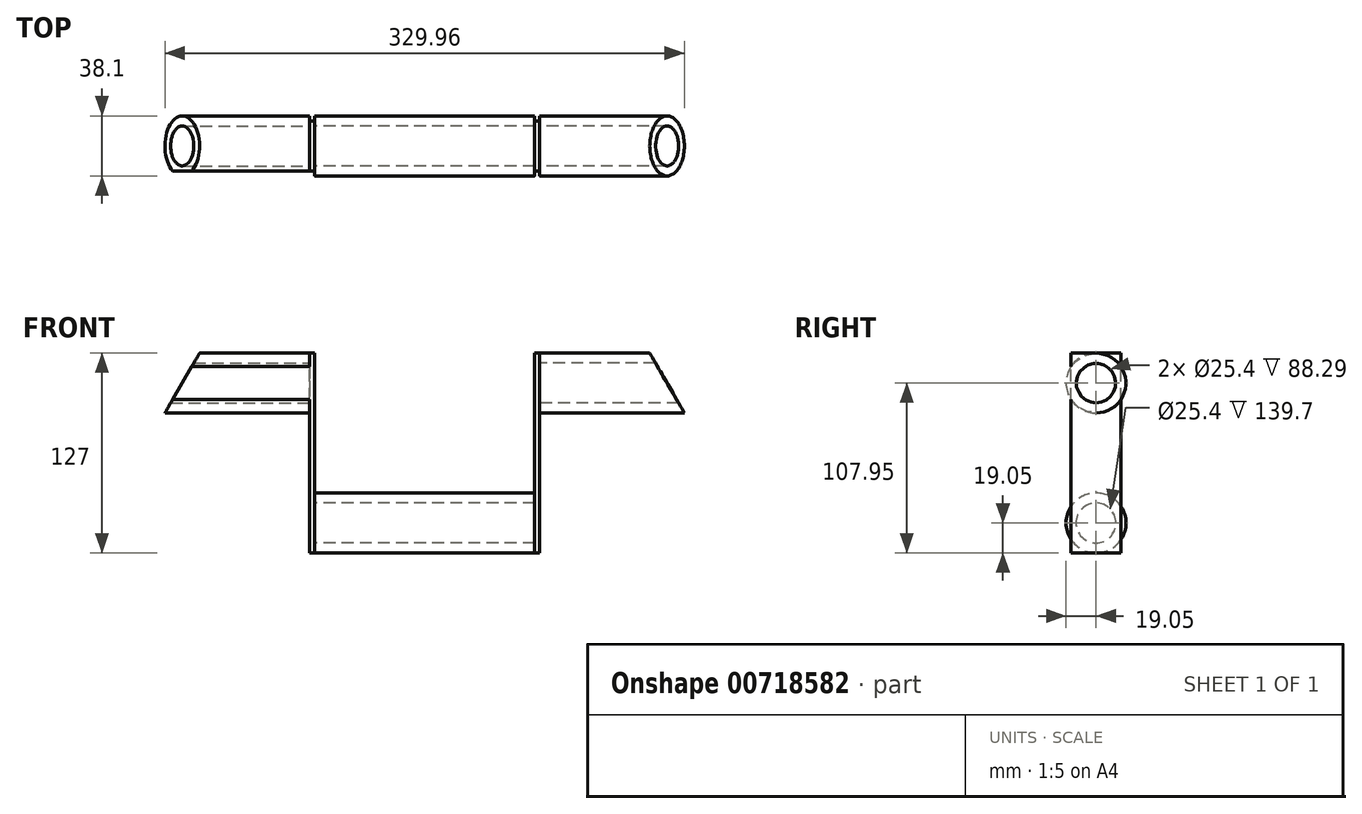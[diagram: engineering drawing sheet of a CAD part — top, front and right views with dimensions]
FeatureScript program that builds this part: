
annotation { "Feature Type Name" : "Feature", "Feature Type Description" : "" }
export const myFeature = defineFeature(function(context is Context, id is Id, definition is map)
    precondition{}
    {
        {
            var Q0;
            Q0=qCreatedBy(makeId("Right.planeOp"),FACE);
            var sketch = newSketch(context, id + "F0", { "sketchPlane" : qUnion([Q0])});
            skCircle(sketch, "E0", {"center": v(0, 0) * mm, "radius": 19.05 * mm});
            skCircle(sketch, "E1", {"center": v(0, 0) * mm, "radius": 12.7 * mm});
            skSolve(sketch);
        }
        {
            var Q0;
            Q0=qCreatedBy(makeId("Front.planeOp"),FACE);
            var sketch = newSketch(context, id + "F1", { "sketchPlane" : qUnion([Q0])});
            skLineSegment(sketch, "E2", {"start": v(0, 0) * mm, "end": v(153.98, 88.9) * mm});
            skLineSegment(sketch, "E3", {"start": v(153.98, 88.9) * mm, "end": v(0, 0) * mm});
            skLineSegment(sketch, "E4", {"start": v(0, 0) * mm, "end": v(-153.98, 88.9) * mm});
            skSolve(sketch);
        }
        {
            var Q0;
            Q0=makeQuery(id+"F0.imprint","IMPRINT",FACE,{"disambiguationData":[TD([[makeQuery(id+"F0.imprint","IMPRINT",EDGE,{"derivedFrom":sQuery(id+"F0.wireOp",EDGE,"E0")}),1.0]])]});
            extrude(context, id + "F2", {"entities" : qUnion([Q0]), "endBound" : BoundingType.SYMMETRIC, "depth" : 139.7 * mm, "offsetDistance" : 25.4 * mm});
        }
        {
            var Q0;
            Q0=makeQuery(id+"F2.opExtrude","CAP_FACE",FACE,{"disambiguationData":[OSD([sQuery(id+"F0.wireOp",EDGE,"E0"),sQuery(id+"F0.wireOp",EDGE,"E1")])],"isStart":false});
            var sketch = newSketch(context, id + "F3", { "sketchPlane" : qUnion([Q0])});
            skLineSegment(sketch, "E5.bottom", {"start": v(15.88, -19.05) * mm, "end": v(-15.88, -19.05) * mm});
            skPoint(sketch, "E5.middle", {"position": v(0, 0) * mm});
            skLineSegment(sketch, "E6", {"start": v(-15.88, -19.05) * mm, "end": v(-15.88, 107.95) * mm});
            skLineSegment(sketch, "E7", {"start": v(15.88, -19.05) * mm, "end": v(15.88, 107.95) * mm});
            skLineSegment(sketch, "E8", {"start": v(-15.88, 107.95) * mm, "end": v(15.88, 107.95) * mm});
            skSolve(sketch);
        }
        {
            var Q0;
            Q0 = qSketchRegion(id + "F3", true);
            extrude(context, id + "F4", {"entities" : qUnion([Q0]), "operationType" : NewBodyOperationType.ADD, "depth" : 3.17 * mm, "offsetDistance" : 25.4 * mm});
        }
        {
            var Q0;
            Q0=makeQuery(id+"F4.opExtrude","CAP_FACE",FACE,{"disambiguationData":[OSD([sQuery(id+"F3.wireOp",EDGE,"E5.bottom"),sQuery(id+"F3.wireOp",EDGE,"E6"),sQuery(id+"F3.wireOp",EDGE,"E7"),sQuery(id+"F3.wireOp",EDGE,"E8")])],"isStart":false});
            var sketch = newSketch(context, id + "F5", { "sketchPlane" : qUnion([Q0])});
            skCircle(sketch, "E9", {"center": v(0, 88.9) * mm, "radius": 19.05 * mm});
            skPoint(sketch, "E9.first.point", {"position": v(0, 107.95) * mm});
            skPoint(sketch, "E9.second.point", {"position": v(0, 69.85) * mm});
            skPoint(sketch, "E9.second.point.positionSnap0", {"position": v(0, 107.95) * mm});
            skPoint(sketch, "E9.third.point", {"position": v(-17.8, 95.7) * mm});
            skCircle(sketch, "E10", {"center": v(0, 88.9) * mm, "radius": 12.7 * mm});
            skSolve(sketch);
        }
        {
            var Q0;
            Q0=makeQuery(id+"F5.imprint","IMPRINT",FACE,{"disambiguationData":[TD([[makeQuery(id+"F5.imprint","IMPRINT",EDGE,{"derivedFrom":sQuery(id+"F5.wireOp",EDGE,"E10")}),-1.0]])]});
            var Q1;
            {var subQ0=sQuery(id+"F5.wireOp",EDGE,"E9");var subQ1=makeQuery(id+"F4.opExtrude","CAP_EDGE",EDGE,{"disambiguationData":[OSD([sQuery(id+"F3.wireOp",EDGE,"E6")])],"isStart":false});var subQ2=makeQuery(id+"F5.imprint","INTERSECT",VERTEX,{"disambiguationData":[OD(0.0)],"derivedFrom":[subQ1,subQ0]});Q1=makeQuery(id+"F5.imprint","IMPRINT",FACE,{"disambiguationData":[TD([[makeQuery(id+"F5.imprint","IMPRINT",EDGE,{"disambiguationData":[TD([[subQ2,-1.0]])],"derivedFrom":subQ0}),1.0]])]});}
            var Q2;
            {var subQ0=sQuery(id+"F5.wireOp",EDGE,"E9");var subQ1=makeQuery(id+"F4.opExtrude","CAP_EDGE",EDGE,{"disambiguationData":[OSD([sQuery(id+"F3.wireOp",EDGE,"E7")])],"isStart":false});var subQ2=makeQuery(id+"F5.imprint","INTERSECT",VERTEX,{"disambiguationData":[OD(0.0)],"derivedFrom":[subQ1,subQ0]});Q2=makeQuery(id+"F5.imprint","IMPRINT",FACE,{"disambiguationData":[TD([[makeQuery(id+"F5.imprint","IMPRINT",EDGE,{"disambiguationData":[TD([[subQ2,1.0]])],"derivedFrom":subQ0}),1.0]])]});}
            extrude(context, id + "F6", {"entities" : qUnion([Q0, Q1, Q2]), "operationType" : NewBodyOperationType.ADD, "depth" : 101.6 * mm, "offsetDistance" : 25.4 * mm});
        }
        {
            var Q0;
            Q0=makeQuery(id+"F2.opExtrude","CAP_FACE",FACE,{"disambiguationData":[OSD([sQuery(id+"F0.wireOp",EDGE,"E0"),sQuery(id+"F0.wireOp",EDGE,"E1")])],"isStart":true});
            var sketch = newSketch(context, id + "F7", { "sketchPlane" : qUnion([Q0])});
            skLineSegment(sketch, "E11.bottom", {"start": v(15.88, -19.05) * mm, "end": v(-15.87, -19.05) * mm});
            skLineSegment(sketch, "E11.top", {"start": v(15.87, 107.95) * mm, "end": v(-15.88, 107.95) * mm});
            skLineSegment(sketch, "E11.left", {"start": v(15.88, -19.05) * mm, "end": v(15.87, 107.95) * mm});
            skLineSegment(sketch, "E11.right", {"start": v(-15.87, -19.05) * mm, "end": v(-15.88, 107.95) * mm});
            skPoint(sketch, "E11.middle", {"position": v(0, 44.45) * mm});
            skSolve(sketch);
        }
        {
            var Q0;
            {var subQ0=sQuery(id+"F7.wireOp",EDGE,"E11.top");Q0=makeQuery(id+"F7.imprint","IMPRINT",FACE,{"disambiguationData":[TD([[makeQuery(id+"F7.imprint","IMPRINT",EDGE,{"derivedFrom":subQ0}),1.0]])]});}
            var Q1;
            {var subQ0=sQuery(id+"F7.wireOp",EDGE,"E11.left");var subQ1=sQuery(id+"F7.wireOp",EDGE,"E11.bottom");var subQ2=makeQuery(id+"F7.imprint","INTERSECT",VERTEX,{"derivedFrom":[subQ1,subQ0]});Q1=makeQuery(id+"F7.imprint","IMPRINT",FACE,{"disambiguationData":[TD([[makeQuery(id+"F7.imprint","IMPRINT",EDGE,{"disambiguationData":[TD([[subQ2,-1.0]])],"derivedFrom":subQ1}),-1.0]])]});}
            var Q2;
            {var subQ0=sQuery(id+"F7.wireOp",EDGE,"E11.right");var subQ1=sQuery(id+"F7.wireOp",EDGE,"E11.bottom");var subQ2=makeQuery(id+"F7.imprint","INTERSECT",VERTEX,{"derivedFrom":[subQ1,subQ0]});Q2=makeQuery(id+"F7.imprint","IMPRINT",FACE,{"disambiguationData":[TD([[makeQuery(id+"F7.imprint","IMPRINT",EDGE,{"disambiguationData":[TD([[subQ2,1.0]])],"derivedFrom":subQ1}),-1.0]])]});}
            var Q3;
            Q3=makeQuery(id+"F7.imprint","IMPRINT",FACE,{"disambiguationData":[TD([[makeQuery(id+"F7.imprint","IMPRINT",EDGE,{"derivedFrom":makeQuery(id+"F2.opExtrude","CAP_EDGE",EDGE,{"disambiguationData":[OSD([sQuery(id+"F0.wireOp",EDGE,"E1")])],"isStart":true})}),1.0]])]});
            var Q4;
            Q4=makeQuery(id+"F7.imprint","IMPRINT",FACE,{"disambiguationData":[TD([[makeQuery(id+"F7.imprint","IMPRINT",EDGE,{"derivedFrom":makeQuery(id+"F2.opExtrude","CAP_EDGE",EDGE,{"disambiguationData":[OSD([sQuery(id+"F0.wireOp",EDGE,"E1")])],"isStart":true})}),-1.0]])]});
            extrude(context, id + "F8", {"entities" : qUnion([Q0, Q1, Q2, Q3, Q4]), "operationType" : NewBodyOperationType.ADD, "depth" : 3.17 * mm, "offsetDistance" : 25.4 * mm});
        }
        {
            var Q0;
            Q0=makeQuery(id+"F8.opExtrude","CAP_FACE",FACE,{"disambiguationData":[OSD([sQuery(id+"F7.wireOp",EDGE,"E11.bottom"),sQuery(id+"F7.wireOp",EDGE,"E11.top"),sQuery(id+"F7.wireOp",EDGE,"E11.left"),sQuery(id+"F7.wireOp",EDGE,"E11.right")])],"isStart":false});
            var sketch = newSketch(context, id + "F9", { "sketchPlane" : qUnion([Q0])});
            skCircle(sketch, "E12", {"center": v(0, 88.9) * mm, "radius": 19.05 * mm});
            skPoint(sketch, "E12.first.point", {"position": v(0, 69.85) * mm});
            skPoint(sketch, "E12.second.point", {"position": v(0, 107.95) * mm});
            skPoint(sketch, "E12.third.point", {"position": v(-15.56, 99.9) * mm});
            skCircle(sketch, "E13", {"center": v(0, 88.9) * mm, "radius": 12.7 * mm});
            skSolve(sketch);
        }
        {
            var Q0;
            Q0=makeQuery(id+"F9.imprint","IMPRINT",FACE,{"disambiguationData":[TD([[makeQuery(id+"F9.imprint","IMPRINT",EDGE,{"derivedFrom":sQuery(id+"F9.wireOp",EDGE,"E13")}),-1.0]])]});
            var Q1;
            {var subQ0=sQuery(id+"F9.wireOp",EDGE,"E12");var subQ1=makeQuery(id+"F8.opExtrude","CAP_EDGE",EDGE,{"disambiguationData":[OSD([sQuery(id+"F7.wireOp",EDGE,"E11.left")])],"isStart":false});var subQ2=makeQuery(id+"F9.imprint","INTERSECT",VERTEX,{"disambiguationData":[OD(0.0)],"derivedFrom":[subQ1,subQ0]});Q1=makeQuery(id+"F9.imprint","IMPRINT",FACE,{"disambiguationData":[TD([[makeQuery(id+"F9.imprint","IMPRINT",EDGE,{"disambiguationData":[TD([[subQ2,1.0]])],"derivedFrom":subQ0}),1.0]])]});}
            var Q2;
            {var subQ0=sQuery(id+"F9.wireOp",EDGE,"E12");var subQ1=makeQuery(id+"F8.opExtrude","CAP_EDGE",EDGE,{"disambiguationData":[OSD([sQuery(id+"F7.wireOp",EDGE,"E11.right")])],"isStart":false});var subQ2=makeQuery(id+"F9.imprint","INTERSECT",VERTEX,{"disambiguationData":[OD(0.0)],"derivedFrom":[subQ1,subQ0]});Q2=makeQuery(id+"F9.imprint","IMPRINT",FACE,{"disambiguationData":[TD([[makeQuery(id+"F9.imprint","IMPRINT",EDGE,{"disambiguationData":[TD([[subQ2,-1.0]])],"derivedFrom":subQ0}),1.0]])]});}
            extrude(context, id + "F10", {"entities" : qUnion([Q0, Q1, Q2]), "operationType" : NewBodyOperationType.ADD, "depth" : 101.6 * mm, "offsetDistance" : 25.4 * mm});
        }
        {
            var Q0;
            Q0=sQuery(id+"F1.wireOp",VERTEX,"E3.start");
            var Q1;
            Q1=sQuery(id+"F1.wireOp",EDGE,"E3");
            cPlane(context, id + "F11", {"entities" : qUnion([Q0, Q1]), "cplaneType" : CPlaneType.LINE_POINT, "offset" : 25.4 * mm, "width" : 152.4 * mm, "height" : 152.4 * mm});
        }
        {
            var Q0;
            Q0=sQuery(id+"F1.wireOp",EDGE,"E4");
            var Q1;
            Q1=sQuery(id+"F1.wireOp",VERTEX,"E4.end");
            cPlane(context, id + "F12", {"entities" : qUnion([Q0, Q1]), "cplaneType" : CPlaneType.LINE_POINT, "offset" : 25.4 * mm, "width" : 152.4 * mm, "height" : 152.4 * mm});
        }
        {
            var Q0;
            Q0=makeQuery(id+"F6.opExtrude","CAP_FACE",FACE,{"disambiguationData":[OSD([sQuery(id+"F5.wireOp",EDGE,"E9"),sQuery(id+"F5.wireOp",EDGE,"E10")])],"isStart":false});
            var Q1;
            Q1=qCreatedBy(id+"F11.planeOp",FACE);
            extrude(context, id + "F13", {"entities" : qUnion([Q0]), "operationType" : NewBodyOperationType.REMOVE, "endBound" : BoundingType.UP_TO_SURFACE, "oppositeDirection" : true, "depth" : 25.4 * mm, "endBoundEntityFace" : qUnion([Q1]), "offsetDistance" : 25.4 * mm});
        }
        {
            var Q0;
            Q0=makeQuery(id+"F10.opExtrude","CAP_FACE",FACE,{"disambiguationData":[OSD([sQuery(id+"F9.wireOp",EDGE,"E12"),sQuery(id+"F9.wireOp",EDGE,"E13")])],"isStart":false});
            var Q1;
            Q1=qCreatedBy(id+"F12.planeOp",FACE);
            extrude(context, id + "F14", {"entities" : qUnion([Q0]), "operationType" : NewBodyOperationType.REMOVE, "endBound" : BoundingType.UP_TO_SURFACE, "oppositeDirection" : true, "depth" : 25.4 * mm, "endBoundEntityFace" : qUnion([Q1]), "offsetDistance" : 25.4 * mm});
        }
    });
